# Revit family: M_Valve_Control_MEPcontent_Oventrop_Cocon QFC 11461
name_source: partatom
category: Pipe Accessories
revit_build: Autodesk Revit 2015 (Build: 20140223_1515(x64)
units: mm (PartAtom-declared; Revit-internal decimal feet)

## types (8) — shared parameters
Aluminium = Color RGB 140-140-140
Angle = 60.00°
Article Description = Flow Control valve
Article Type = Cocon QFC 11461
Bonnet = Color RGB 35-35-35
Bronze = Color RGB 156-122-90
Content Supplier URL = www.mepcontent.eu
Custom = No
Description = Flow Control valve
EMCS Version = 2.0
ETIM Article Class = EC011435
Family Version = 10.14
IFCExportAs = IfcValveType
IFCExportType = REGULATING
L2 = 38 mm  [stored 0.124672 ft]
Lgt1 = 3 mm  [stored 0.00984252 ft]
MEPcontent Class = VALVE_CONTROL
Manufacturer = Oventrop
Manufacturer URL = http://www.oventrop.de
Model = Cocon QFC 11461
Product Line = Oventrop
Ra1 = 8 mm  [stored 0.0262467 ft]
Ra2 = 6 mm  [stored 0.019685 ft]
Ra3 = 5 mm  [stored 0.0164042 ft]
Ra4 = 15 mm  [stored 0.0492126 ft]
Revit Version = 2015
URL = www.stabiplan.com
r1 = 2 mm  [stored 0.00656168 ft]
r2 = 3 mm  [stored 0.00984252 ft]

## per-type parameters (varying)
- DN 40: Arrow1=4 mm  [stored 0.0131234 ft]; FlangeDiameter=150 mm; GTIN=4026755372465; Hb1=285 mm; Hb3=11 mm  [stored 0.0360892 ft]; Hb4=5 mm  [stored 0.0164042 ft]; Hb5=4 mm  [stored 0.0131234 ft]; Hb6=10 mm  [stored 0.0328084 ft]; Height=250 mm; L1=200 mm; Length=200 mm; Length_B=11 mm  [stored 0.0360892 ft]; Length_C=19 mm; Length_D=14 mm  [stored 0.0459318 ft]; Lgt2=12 mm  [stored 0.0393701 ft]; Lgt3=25 mm  [stored 0.082021 ft]; Manufacturer Art. No.=1146149; Nominal Diameter=40 mm; OuterDiameter=48 mm; Rad1=50 mm; Rad2=75 mm; Rad3=38 mm  [stored 0.124672 ft]; Rad4=32 mm; RadiusPressure=22 mm  [stored 0.0721785 ft]; Rb1=32 mm; Safe_Length=32 mm
- DN 50: Arrow1=5 mm  [stored 0.0164042 ft]; FlangeDiameter=165 mm; GTIN=4026755355246; Hb1=308 mm; Hb3=15 mm  [stored 0.0492126 ft]; Hb4=7 mm  [stored 0.0229659 ft]; Hb5=5 mm  [stored 0.0164042 ft]; Hb6=14 mm  [stored 0.0459318 ft]; Height=270 mm; L1=230 mm; Length=230 mm; Length_B=12 mm  [stored 0.0393701 ft]; Length_C=21 mm; Length_D=15 mm  [stored 0.0492126 ft]; Lgt2=14 mm  [stored 0.0459318 ft]; Lgt3=29 mm; Manufacturer Art. No.=1146150; Nominal Diameter=50 mm; OuterDiameter=60 mm; Rad1=55 mm; Rad2=83 mm; Rad3=42 mm; Rad4=36 mm; RadiusPressure=26 mm  [stored 0.0853018 ft]; Rb1=36 mm; Safe_Length=36 mm
- DN 65: Arrow1=6 mm  [stored 0.019685 ft]; FlangeDiameter=185 mm; GTIN=4026755355253; Hb1=423 mm; Hb3=35 mm  [stored 0.114829 ft]; Hb4=16 mm; Hb5=12 mm  [stored 0.0393701 ft]; Hb6=32 mm; Height=370 mm; L1=290 mm; Length=290 mm; Length_B=17 mm  [stored 0.0557743 ft]; Length_C=28 mm  [stored 0.0918635 ft]; Length_D=21 mm; Lgt2=17 mm  [stored 0.0557743 ft]; Lgt3=36 mm; Manufacturer Art. No.=1146151; Nominal Diameter=65 mm; OuterDiameter=76 mm; Rad1=61 mm; Rad2=93 mm; Rad3=47 mm; Rad4=40 mm  [stored 0.131234 ft]; RadiusPressure=30 mm  [stored 0.0984252 ft]; Rb1=40 mm  [stored 0.131234 ft]; Safe_Length=40 mm  [stored 0.131234 ft]
- DN 80: Arrow1=6 mm  [stored 0.019685 ft]; FlangeDiameter=200 mm; GTIN=4026755355260; Hb1=441 mm; Hb3=38 mm  [stored 0.124672 ft]; Hb4=17 mm  [stored 0.0557743 ft]; Hb5=13 mm; Hb6=35 mm  [stored 0.114829 ft]; Height=385 mm; L1=310 mm; Length=310 mm; Length_B=18 mm; Length_C=29 mm; Length_D=22 mm  [stored 0.0721785 ft]; Lgt2=19 mm; Lgt3=39 mm; Manufacturer Art. No.=1146152; Nominal Diameter=80 mm; OuterDiameter=89 mm; Rad1=66 mm; Rad2=100 mm; Rad3=51 mm; Rad4=43 mm  [stored 0.141076 ft]; RadiusPressure=33 mm  [stored 0.108268 ft]; Rb1=43 mm  [stored 0.141076 ft]; Safe_Length=43 mm  [stored 0.141076 ft]
- DN 100: Arrow1=7 mm  [stored 0.0229659 ft]; FlangeDiameter=220 mm; GTIN=4026755355277; Hb1=464 mm; Hb3=42 mm; Hb4=19 mm; Hb5=14 mm  [stored 0.0459318 ft]; Hb6=38 mm  [stored 0.124672 ft]; Height=405 mm; L1=350 mm; Length=350 mm; Length_B=19 mm; Length_C=31 mm; Length_D=23 mm; Lgt2=21 mm; Lgt3=44 mm; Manufacturer Art. No.=1146153; Nominal Diameter=100 mm; OuterDiameter=114 mm; Rad1=73 mm; Rad2=110 mm; Rad3=56 mm; Rad4=47 mm; RadiusPressure=37 mm; Rb1=47 mm; Safe_Length=47 mm
- DN 125: Arrow1=8 mm  [stored 0.0262467 ft]; FlangeDiameter=250 mm; GTIN=4026755355284; Hb1=596 mm; Hb3=65 mm; Hb4=30 mm  [stored 0.0984252 ft]; Hb5=22 mm  [stored 0.0721785 ft]; Hb6=59 mm; Height=520 mm; L1=400 mm; Length=400 mm; Length_B=24 mm  [stored 0.0787402 ft]; Length_C=40 mm  [stored 0.131234 ft]; Length_D=30 mm  [stored 0.0984252 ft]; Lgt2=24 mm  [stored 0.0787402 ft]; Lgt3=50 mm; Manufacturer Art. No.=1146154; Nominal Diameter=125 mm; OuterDiameter=140 mm; Rad1=83 mm; Rad2=125 mm; Rad3=63 mm; Rad4=54 mm; RadiusPressure=34 mm; Rb1=54 mm; Safe_Length=54 mm
- DN 150: Arrow1=10 mm  [stored 0.0328084 ft]; FlangeDiameter=285 mm; GTIN=4026755355291; Hb1=596 mm; Hb3=65 mm; Hb4=30 mm  [stored 0.0984252 ft]; Hb5=22 mm  [stored 0.0721785 ft]; Hb6=59 mm; Height=520 mm; L1=480 mm; Length=480 mm; Length_B=24 mm  [stored 0.0787402 ft]; Length_C=40 mm  [stored 0.131234 ft]; Length_D=30 mm  [stored 0.0984252 ft]; Lgt2=29 mm; Lgt3=60 mm; Manufacturer Art. No.=1146155; Nominal Diameter=150 mm; OuterDiameter=168 mm; Rad1=94 mm; Rad2=143 mm; Rad3=72 mm; Rad4=61 mm; RadiusPressure=41 mm; Rb1=61 mm; Safe_Length=61 mm
- DN 200: Arrow1=12 mm  [stored 0.0393701 ft]; FlangeDiameter=340 mm; GTIN=4026755391176; Hb1=648 mm; Hb3=74 mm; Hb4=34 mm; Hb5=25 mm  [stored 0.082021 ft]; Hb6=67 mm; Height=565 mm; L1=600 mm; Length=600 mm; Length_B=26 mm  [stored 0.0853018 ft]; Length_C=43 mm  [stored 0.141076 ft]; Length_D=32 mm; Lgt2=36 mm; Lgt3=75 mm; Manufacturer Art. No.=1146156; Nominal Diameter=200 mm; OuterDiameter=219 mm; Rad1=112 mm; Rad2=170 mm; Rad3=86 mm; Rad4=73 mm; RadiusPressure=53 mm; Rb1=73 mm; Safe_Length=73 mm

note: [stored X ft] marks values corroborated as IEEE doubles in the binary element streams (Revit-internal decimal feet)

## geometry (parser evidence)
native form markers: Sweep x2
no freeform markers — native parametric forms only
